# Revit family: LR2140-W-2-RM
name_source: partatom
category: Plumbing Fixtures
revit_build: Autodesk Revit MEP 2016 (Build: 20150220_1215(x64)
units: mm (PartAtom-declared; Revit-internal decimal feet)

## family parameters
Cut with Voids When Loaded = No
Host = Face
OmniClass Number = 23.45.05.21.11.11
OmniClass Title = Water Operated Water Closets
Part Type = Normal
Room Calculation Point = No
Round Connector Dimension = Use Diameter
Shared = Yes

## types (2) — shared parameters
2- On Floor, Wall Outlet Toilet = No
CW Connection = Yes
Material = Stainless Steel
RM- Rear Mount = Yes
Tempered Water Connection = No
Vent Connection = No
W- Wall (Concealed) = Yes
Waste Connection = Yes
zero-valued in all types: Amperage, CWFU, HWFU, Voltage, WFU

## per-type parameters (varying)
- LR2140-W-2-RM: - 1.28 GPF (HET)=No; - 1.6 GPF=No; ADA- 18" ADA Integral Seat Height=No; CO1- Cleanout with O-Ring to NO-Hub 2-3/8" x 4"=No; CO1_3 - Cleanout with O-Ring to NO-Hub 2-3/8" x 3"=No; Default Elevation=15"; Description=Ligature Resistant BlowOut Jet Toilet; EG- Enviro-Glaze Color   Toilet Exterior Only   Toilet Interior=No; FG- 14 Gage=No; FV- Flush Valve, Mechanical (N/A for ADA)=No; FVBO- Flush Valv by Others=No; FVH- Flush Valve, Hydraulic (N/A for Top Supply)=No; FVT- Flush Valve Thru-Wall Connection=No; GW- Gasket Waste=No; HP- High Polish Finish (Exterior Only)=No; HW Connection=No; MT- Metal Template=No; MVCFV- Time-trol Electronic F.V. (N/A for Top Supply)=No; Manufacturer=Acorn Engineering Co.; Model=2140-W-2-RM; PC- Pinned Cleanout Plug=No; Revised Date=09/20/18; SW- Wall Sleeve=No; T- Top (Exposed ) (LRFVC Required)=No; TF- Time-Trol Transformer=No; URL=https://www.acorneng.com; VAC- Acorn Vac System=No
- Must Match Filename: - 1.28 GPF (HET)=Yes; - 1.6 GPF=Yes; ADA- 18" ADA Integral Seat Height=Yes; CO1- Cleanout with O-Ring to NO-Hub 2-3/8" x 4"=Yes; CO1_3 - Cleanout with O-Ring to NO-Hub 2-3/8" x 3"=Yes; Default Elevation=34"; Description=Description Must Match Submittal Description; EG- Enviro-Glaze Color   Toilet Exterior Only   Toilet Interior=Yes; FG- 14 Gage=Yes; FV- Flush Valve, Mechanical (N/A for ADA)=Yes; FVBO- Flush Valv by Others=Yes; FVH- Flush Valve, Hydraulic (N/A for Top Supply)=Yes; FVT- Flush Valve Thru-Wall Connection=Yes; GW- Gasket Waste=Yes; HP- High Polish Finish (Exterior Only)=Yes; HW Connection=Yes; MT- Metal Template=Yes; MVCFV- Time-trol Electronic F.V. (N/A for Top Supply)=Yes; Manufacturer=Use appropriate company name, refer to Acorn-Revit Style Guide; Model=Model#-Options, example:  1415-CT-1; PC- Pinned Cleanout Plug=Yes; Revised Date=example:  05/28/11; SW- Wall Sleeve=Yes; T- Top (Exposed ) (LRFVC Required)=Yes; TF- Time-Trol Transformer=Yes; URL=Use appropriate URL, refer to Acorn-Revit Style Guide; VAC- Acorn Vac System=Yes

## geometry (parser evidence)
native form markers: Sweep x1
no freeform markers — native parametric forms only
